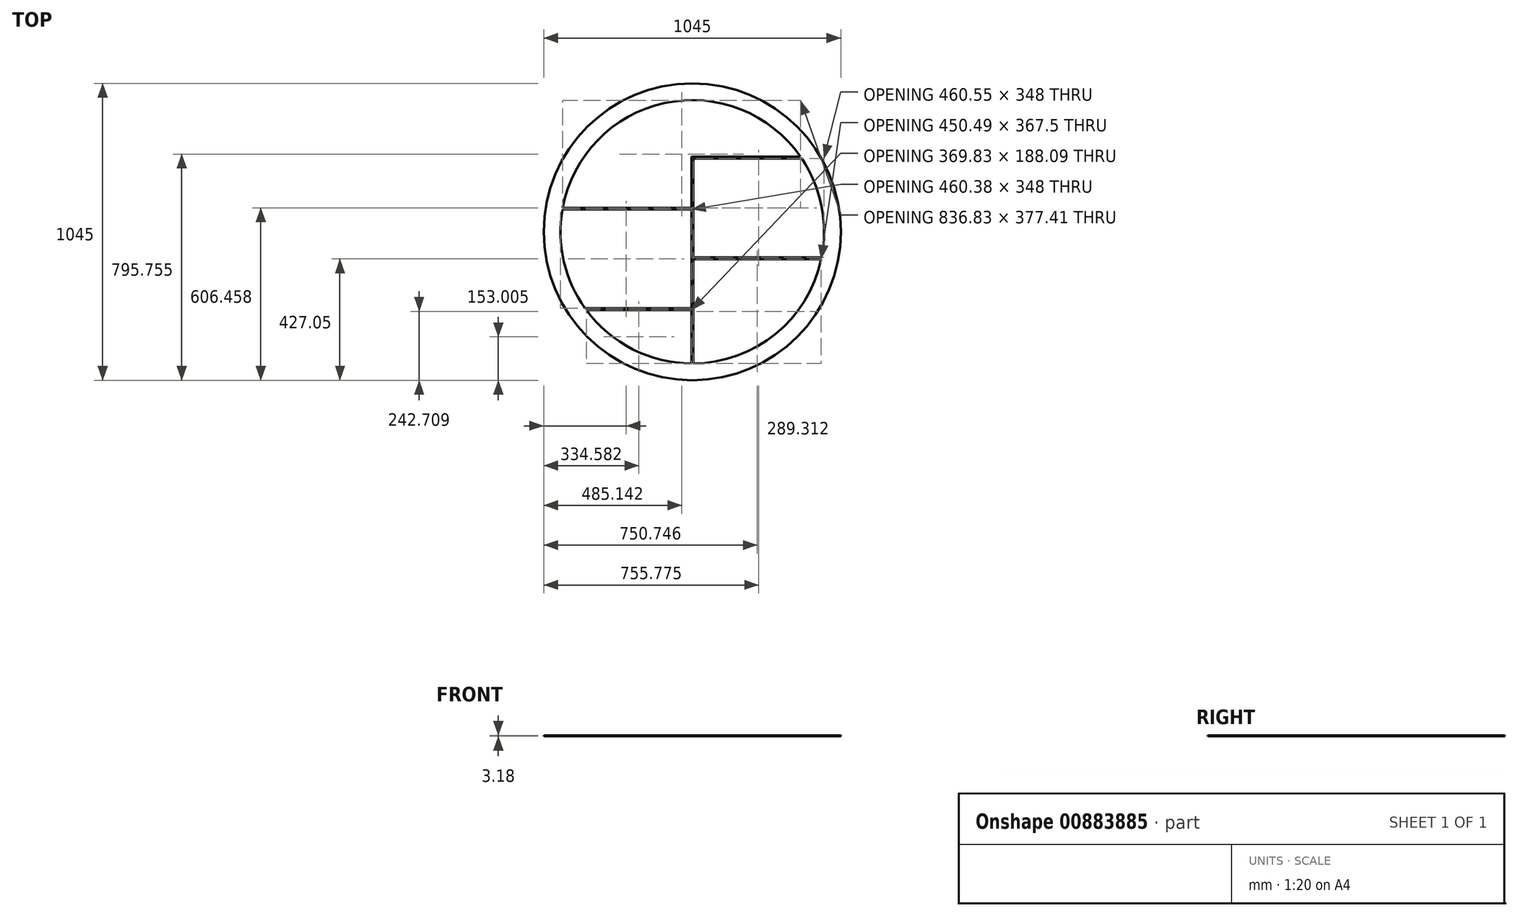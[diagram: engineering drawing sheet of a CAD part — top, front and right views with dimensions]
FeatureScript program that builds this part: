
annotation { "Feature Type Name" : "Feature", "Feature Type Description" : "" }
export const myFeature = defineFeature(function(context is Context, id is Id, definition is map)
    precondition{}
    {
        {
            var Q0;
            Q0=qCreatedBy(makeId("Top.planeOp"),FACE);
            var sketch = newSketch(context, id + "F0", { "sketchPlane" : qUnion([Q0])});
            skCircle(sketch, "E0", {"center": v(0, 0) * mm, "radius": 463.55 * mm});
            skCircle(sketch, "E1", {"center": v(0, 0) * mm, "radius": 522.5 * mm});
            skLineSegment(sketch, "E2", {"start": v(-568.84, 0) * mm, "end": v(644.11, 0) * mm, "construction": true});
            skLineSegment(sketch, "E3", {"start": v(0, 577.45) * mm, "end": v(0, -594.01) * mm, "construction": true});
            skLineSegment(sketch, "E4", {"start": v(0, 463.55) * mm, "end": v(309.69, 452.96) * mm, "construction": true});
            skLineSegment(sketch, "E5", {"start": v(-3, 263.96) * mm, "end": v(-3, -463.54) * mm});
            skLineSegment(sketch, "E6", {"start": v(3, 257.96) * mm, "end": v(3, -463.54) * mm});
            skLineSegment(sketch, "E7", {"start": v(-3, 263.96) * mm, "end": v(381.06, 263.96) * mm});
            skLineSegment(sketch, "E8", {"start": v(3, 257.96) * mm, "end": v(385.14, 257.96) * mm});
            skLineSegment(sketch, "E9", {"start": v(-3, -269.45) * mm, "end": v(-377.2, -269.45) * mm});
            skLineSegment(sketch, "E10", {"start": v(-3, -275.45) * mm, "end": v(-372.83, -275.45) * mm});
            skLineSegment(sketch, "E11", {"start": v(3, -90.04) * mm, "end": v(454.72, -90.04) * mm});
            skLineSegment(sketch, "E12", {"start": v(3, -96.04) * mm, "end": v(453.5, -96.04) * mm});
            skLineSegment(sketch, "E13", {"start": v(-3, 84.55) * mm, "end": v(-455.77, 84.55) * mm});
            skLineSegment(sketch, "E14", {"start": v(-3, 78.55) * mm, "end": v(-456.85, 78.55) * mm});
            skPoint(sketch, "E15", {"position": v(0, 463.55) * mm});
            skSolve(sketch);
        }
        {
            var Q0;
            Q0 = qSketchRegion(id + "F0", true);
            var Q1;
            {var subQ0=sQuery(id+"F0.wireOp",EDGE,"E13");Q1=makeQuery(id+"F0.imprint","IMPRINT",FACE,{"disambiguationData":[TD([[makeQuery(id+"F0.imprint","IMPRINT",EDGE,{"derivedFrom":subQ0}),1.0]])]});}
            var Q2;
            {var subQ11=sQuery(id+"F0.wireOp",EDGE,"E7");Q2=makeQuery(id+"F0.imprint","IMPRINT",FACE,{"disambiguationData":[TD([[makeQuery(id+"F0.imprint","IMPRINT",EDGE,{"derivedFrom":subQ11}),-1.0]])]});}
            var Q3;
            {var subQ0=sQuery(id+"F0.wireOp",EDGE,"E11");Q3=makeQuery(id+"F0.imprint","IMPRINT",FACE,{"disambiguationData":[TD([[makeQuery(id+"F0.imprint","IMPRINT",EDGE,{"derivedFrom":subQ0}),-1.0]])]});}
            var Q4;
            {var subQ0=sQuery(id+"F0.wireOp",EDGE,"E9");Q4=makeQuery(id+"F0.imprint","IMPRINT",FACE,{"disambiguationData":[TD([[makeQuery(id+"F0.imprint","IMPRINT",EDGE,{"derivedFrom":subQ0}),1.0]])]});}
            extrude(context, id + "F1", {"entities" : qUnion([Q0, Q1, Q2, Q3, Q4]), "depth" : 3.18 * mm, "offsetDistance" : 25 * mm});
        }
    });
